# Revit family: Shower-Handshower_Kit-KOHLER-ACCLIV-K-33097T_1
name_source: partatom
category: Plumbing Fixtures
units: mm (PartAtom-declared; Revit-internal decimal feet)

## family parameters
Cut with Voids When Loaded = No
Host = Face
OmniClass Number = 23.31.17.00
OmniClass Title = Showers
Part Type = Normal
Room Calculation Point = No
Round Connector Dimension = Use Diameter
Shared = No

## types (4) — shared parameters
ADA Compliant = No
Assembly Code = D2010700
CW Connection = Yes
Cold Water Inlet = Cold Water Inlet
Date Modified = 11/22/2022
Default Elevation = 42"
Description = Exposed Shower Faucet - Dome  6P
Drain Included = No
Flow Rate = 0 GPM
HW Connection = Yes
Handle Clearance = 3 7/8"
Height = 2 5/8"
Hot Water Inlet = Hot Water Inlet
Length = 6 3/8"
Manufacturer = Kohler Co.
Master Format 2014 = 22 42 23
Master Format 2014 Name = Residential Showers
Material = Premium Metal Construction
Pressure = 0.00 psi
Product Name = ACCLIV
URL = http://www.kohler.com.cn
Vent Connection = No
Waste Connection = No
Waste Water Outlet = Waste Water Outlet
WaterSense Certified = No
Width = 5 15/16"

## per-type parameters (varying)
| type | Finish | Model | Secondary Finish | Type |
| AF-Vibrant French Gold | Kohler-Metal-AF-Vibrant_French_Gold | K-33097T-4-AF | Kohler-Plastic-95-Ice_Grey | 1 |
| BL-Matte Black | Kohler-Metal-BL-Matte_Black | K-33097T-4-BL | Kohler-Metal-7-Black_Black | 2 |
| BN-Vibrant Brushed Nickel | Kohler-Metal-BN-Vibrant_Brushed_Nickel | K-33097T-4-BN | Kohler-Plastic-95-Ice_Grey | 3 |
| CP-Polished Chrome | Kohler-Metal-CP-Polished_Chrome | K-33097T-4-CP | Kohler-Plastic-95-Ice_Grey | 4 |

## geometry (parser evidence)
native form markers: Sweep x6
no freeform markers — native parametric forms only
